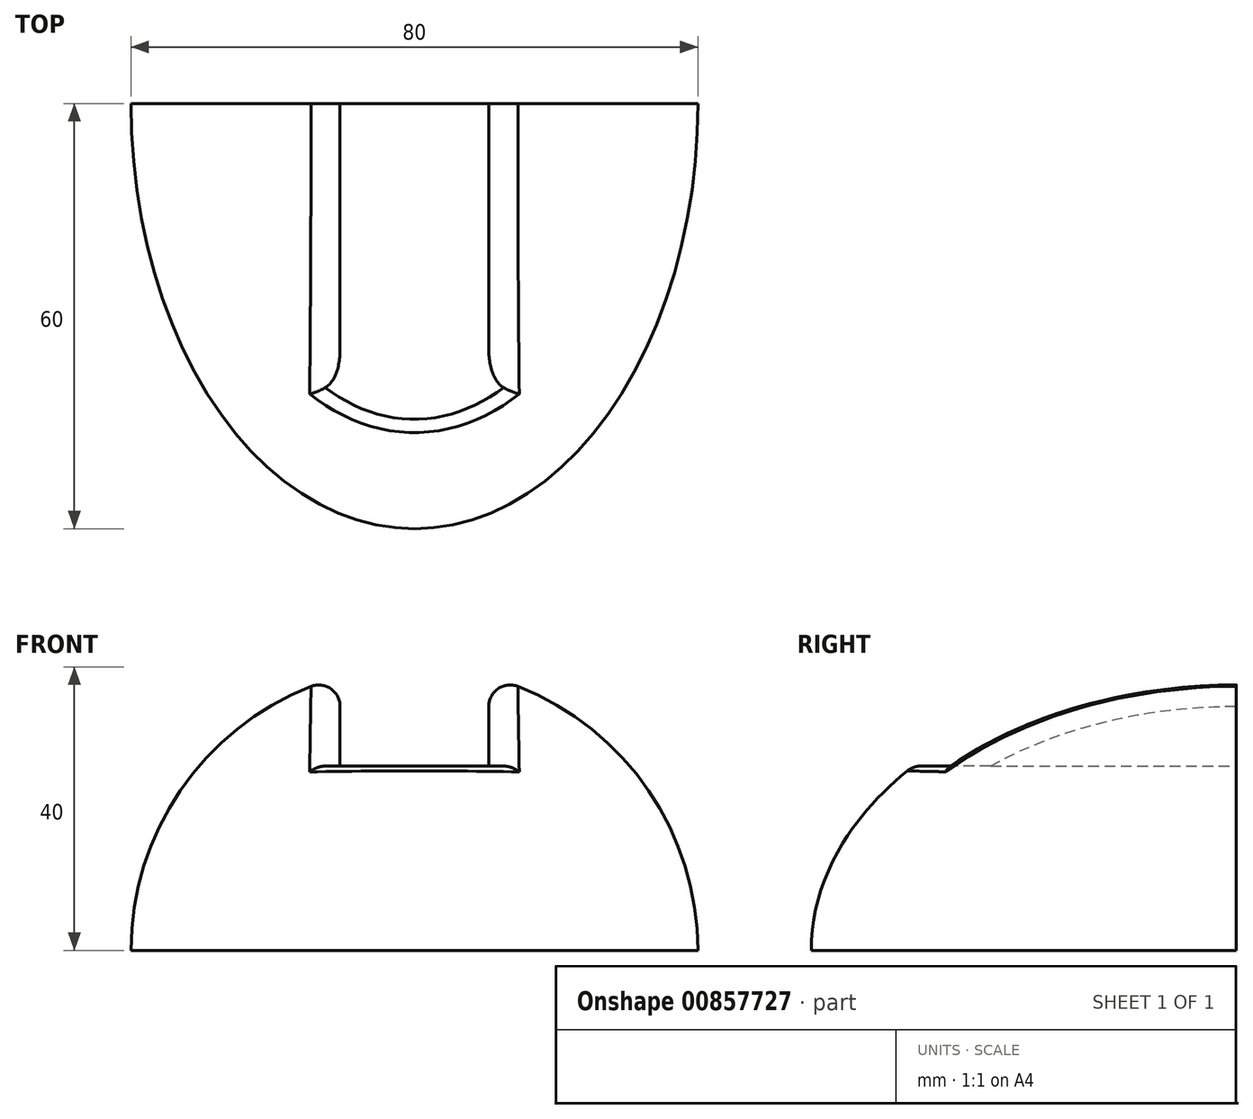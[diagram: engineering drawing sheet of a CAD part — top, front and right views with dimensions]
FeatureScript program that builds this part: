
annotation { "Feature Type Name" : "Feature", "Feature Type Description" : "" }
export const myFeature = defineFeature(function(context is Context, id is Id, definition is map)
    precondition{}
    {
        {
            var Q0;
            Q0=qCreatedBy(makeId("Right.planeOp"),FACE);
            var sketch = newSketch(context, id + "F0", { "sketchPlane" : qUnion([Q0])});
            skEllipticalArc(sketch, "E0", {});
            skLineSegment(sketch, "E1", {"start": v(-60, 0) * mm, "end": v(60, 0) * mm});
            const initialGuessF0  = {"E0": [0, 0, 0, 1, 0.04, 0.06, 4.71238898038469, 1.5707963267948966]};
            skSetInitialGuess(sketch, initialGuessF0);
            skSolve(sketch);
        }
        {
            var Q0;
            Q0 = qSketchRegion(id + "F0", true);
            var Q1;
            Q1=sQuery(id+"F0.wireOp",EDGE,"E1");
            revolve(context, id + "F1", {"surfaceOperationType" : NewSurfaceOperationType.NEW, "entities" : qUnion([Q0]), "axis" : qUnion([Q1]), "revolveType" : RevolveType.SYMMETRIC, "angle" : 180 * degree});
        }
        {
            var Q0;
            Q0=qCreatedBy(makeId("Top.planeOp"),FACE);
            cPlane(context, id + "F2", {"entities" : qUnion([Q0]), "cplaneType" : CPlaneType.OFFSET, "offset" : 26 * mm, "width" : 150 * mm, "height" : 150 * mm});
        }
        {
            var Q0;
            Q0=qCreatedBy(id+"F2.planeOp",FACE);
            var sketch = newSketch(context, id + "F3", { "sketchPlane" : qUnion([Q0])});
            skLineSegment(sketch, "E2.bottom", {"start": v(10.5, -100) * mm, "end": v(-10.5, -100) * mm});
            skLineSegment(sketch, "E2.top", {"start": v(10.5, 100) * mm, "end": v(-10.5, 100) * mm});
            skLineSegment(sketch, "E2.left", {"start": v(10.5, -100) * mm, "end": v(10.5, 100) * mm});
            skLineSegment(sketch, "E2.right", {"start": v(-10.5, -100) * mm, "end": v(-10.5, 100) * mm});
            skPoint(sketch, "E2.middle", {"position": v(0, 0) * mm});
            skSolve(sketch);
        }
        {
            var Q0;
            Q0 = qSketchRegion(id + "F3", true);
            extrude(context, id + "F4", {"entities" : qUnion([Q0]), "operationType" : NewBodyOperationType.REMOVE, "endBound" : BoundingType.THROUGH_ALL, "depth" : 25 * mm, "offsetDistance" : 25 * mm});
        }
        {
            var Q0;
            Q0=qCreatedBy(makeId("Top.planeOp"),FACE);
            var sketch = newSketch(context, id + "F5", { "sketchPlane" : qUnion([Q0])});
            skLineSegment(sketch, "E3.bottom", {"start": v(-193.83, 0) * mm, "end": v(210.63, 0) * mm});
            skLineSegment(sketch, "E3.top", {"start": v(-193.83, 200) * mm, "end": v(210.63, 200) * mm});
            skLineSegment(sketch, "E3.left", {"start": v(-193.83, 0) * mm, "end": v(-193.83, 200) * mm});
            skLineSegment(sketch, "E3.right", {"start": v(210.63, 0) * mm, "end": v(210.63, 200) * mm});
            skSolve(sketch);
        }
        {
            var Q0;
            Q0 = qSketchRegion(id + "F5", true);
            extrude(context, id + "F6", {"entities" : qUnion([Q0]), "operationType" : NewBodyOperationType.REMOVE, "endBound" : BoundingType.THROUGH_ALL, "depth" : 25 * mm, "offsetDistance" : 25 * mm});
        }
        {
            var Q0;
            Q0=makeQuery(id+"F4.boolean.opBoolean","INTERSECT",EDGE,{"derivedFrom":[makeQuery(id+"F1.opRevolve","SWEPT_FACE",FACE,{"disambiguationData":[OSD([sQuery(id+"F0.wireOp",EDGE,"E0")])]}),makeQuery(id+"F4.opExtrude","SWEPT_FACE",FACE,{"disambiguationData":[OSD([sQuery(id+"F3.wireOp",EDGE,"E2.right")])]})]});
            var Q1;
            Q1=makeQuery(id+"F4.boolean.opBoolean","INTERSECT",EDGE,{"derivedFrom":[makeQuery(id+"F1.opRevolve","SWEPT_FACE",FACE,{"disambiguationData":[OSD([sQuery(id+"F0.wireOp",EDGE,"E0")])]}),makeQuery(id+"F4.opExtrude","SWEPT_FACE",FACE,{"disambiguationData":[OSD([sQuery(id+"F3.wireOp",EDGE,"E2.left")])]})]});
            var Q2;
            Q2=makeQuery(id+"F4.boolean.opBoolean","INTERSECT",EDGE,{"disambiguationData":[OD(0.0)],"derivedFrom":[makeQuery(id+"F1.opRevolve","SWEPT_FACE",FACE,{"disambiguationData":[OSD([sQuery(id+"F0.wireOp",EDGE,"E0")])]}),makeQuery(id+"F4.opExtrude","CAP_FACE",FACE,{"disambiguationData":[OSD([sQuery(id+"F3.wireOp",EDGE,"E2.bottom"),sQuery(id+"F3.wireOp",EDGE,"E2.top"),sQuery(id+"F3.wireOp",EDGE,"E2.left"),sQuery(id+"F3.wireOp",EDGE,"E2.right")])],"isStart":true})]});
            fillet(context, id + "F7", {"entities" : qUnion([Q0, Q1, Q2]), "radius" : 3 * mm, "tangentPropagation" : true, "allowEdgeOverflow" : false});
        }
    });
